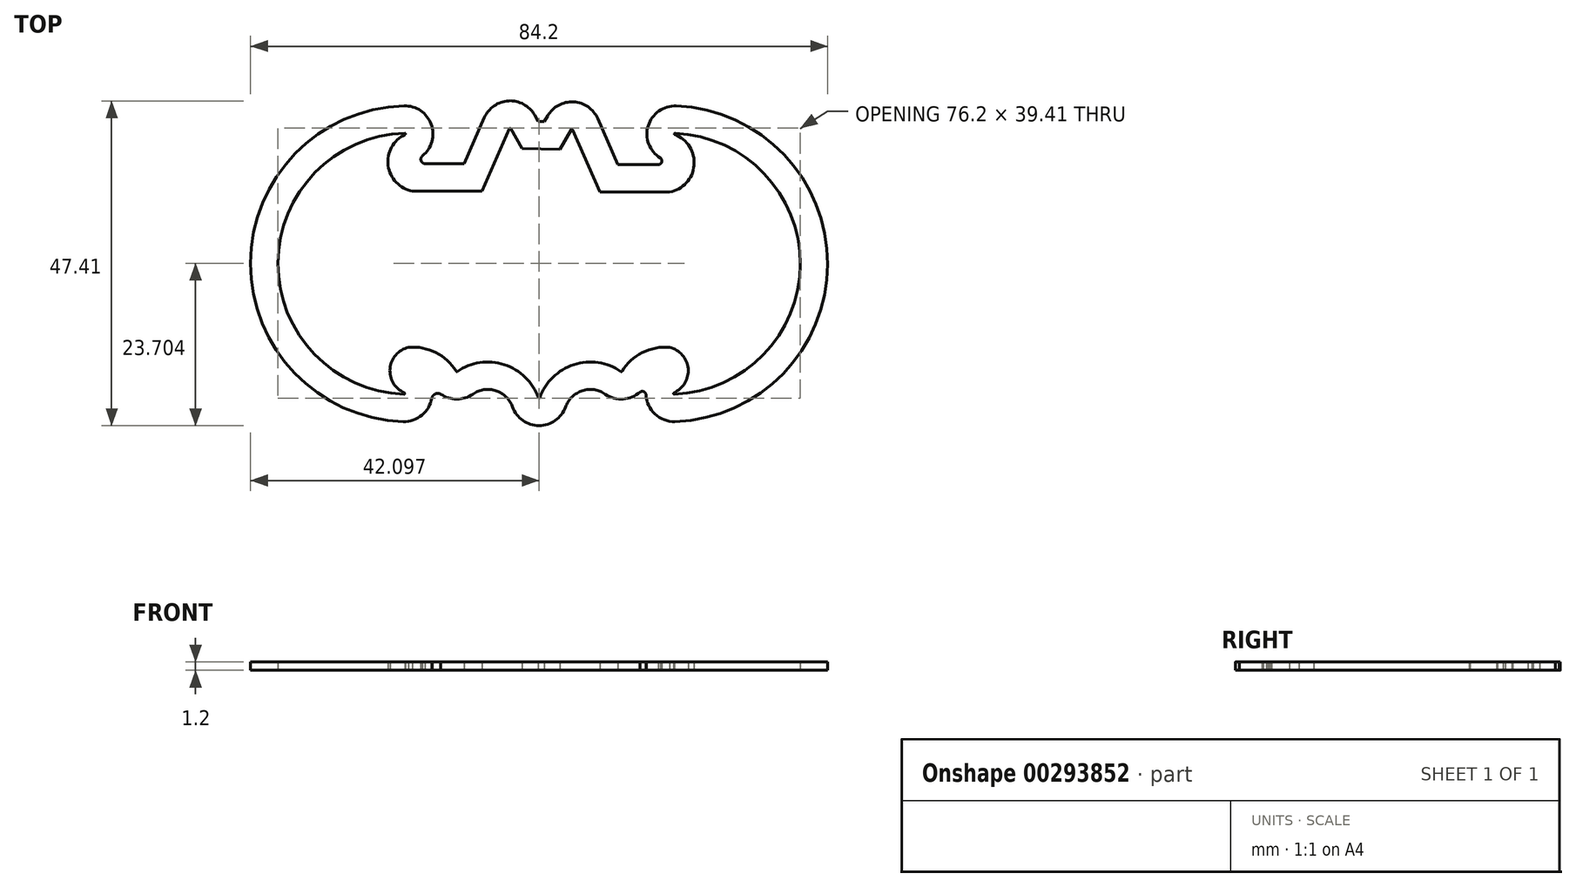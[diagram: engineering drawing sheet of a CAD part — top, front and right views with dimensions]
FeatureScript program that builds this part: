
annotation { "Feature Type Name" : "Feature", "Feature Type Description" : "" }
export const myFeature = defineFeature(function(context is Context, id is Id, definition is map)
    precondition{}
    {
        {
            var Q0;
            Q0=qCreatedBy(makeId("Top.planeOp"),FACE);
            var sketch = newSketch(context, id + "F0", { "sketchPlane" : qUnion([Q0])});
            skArc(sketch, "E0", {"start": v(-14, 19.19) * mm, "mid": v(-32.51, 0.2) * mm, "end": v(-14.11, -18.9) * mm});
            skArc(sketch, "E1", {"start": v(25.28, -18.9) * mm, "mid": v(43.69, 0.08) * mm, "end": v(25.43, 19.18) * mm});
            skArc(sketch, "E2", {"start": v(-13.96, 19) * mm, "mid": v(-16.43, 14.48) * mm, "end": v(-12.89, 10.74) * mm});
            skArc(sketch, "E3.MirrorCS", {"start": v(25.39, 18.99) * mm, "mid": v(28.2, 14.5) * mm, "end": v(24.64, 10.6) * mm});
            skArc(sketch, "E4", {"start": v(-13.46, -12.05) * mm, "mid": v(-16.16, -15.16) * mm, "end": v(-14.07, -18.7) * mm});
            skArc(sketch, "E5.MirrorCS", {"start": v(24.64, -12.05) * mm, "mid": v(27.33, -15.16) * mm, "end": v(25.24, -18.7) * mm});
            skArc(sketch, "E6", {"start": v(-6.5, -15.57) * mm, "mid": v(-9.48, -12.82) * mm, "end": v(-13.46, -12.05) * mm});
            skArc(sketch, "E7", {"start": v(5.5, -19.43) * mm, "mid": v(0.51, -14.58) * mm, "end": v(-6.36, -15.6) * mm});
            skArc(sketch, "E8.MirrorCS", {"start": v(5.68, -19.43) * mm, "mid": v(10.66, -14.58) * mm, "end": v(17.53, -15.6) * mm});
            skArc(sketch, "E9.MirrorCS", {"start": v(17.68, -15.57) * mm, "mid": v(20.66, -12.82) * mm, "end": v(24.64, -12.05) * mm});
            skLineSegment(sketch, "E10", {"start": v(-12.89, 10.74) * mm, "end": v(-2.73, 10.74) * mm});
            skLineSegment(sketch, "E11", {"start": v(-2.73, 10.74) * mm, "end": v(1.27, 19.86) * mm});
            skLineSegment(sketch, "E12", {"start": v(1.45, 19.87) * mm, "end": v(3.1, 16.98) * mm});
            skLineSegment(sketch, "E13.MirrorCS", {"start": v(10.3, 19.72) * mm, "end": v(8.65, 16.83) * mm});
            skLineSegment(sketch, "E14.MirrorCS", {"start": v(14.48, 10.6) * mm, "end": v(10.48, 19.71) * mm});
            skLineSegment(sketch, "E15.MirrorCS", {"start": v(24.64, 10.6) * mm, "end": v(14.48, 10.6) * mm});
            skLineSegment(sketch, "E16", {"start": v(3.1, 16.98) * mm, "end": v(8.65, 16.83) * mm});
            skArc(sketch, "E17.filletArc", {"start": v(5.5, -19.43) * mm, "mid": v(5.59, -19.5) * mm, "end": v(5.68, -19.43) * mm});
            skArc(sketch, "E18.filletArc", {"start": v(25.24, -18.7) * mm, "mid": v(25.18, -18.81) * mm, "end": v(25.28, -18.9) * mm});
            skArc(sketch, "E19.filletArc", {"start": v(-14.11, -18.9) * mm, "mid": v(-14, -18.81) * mm, "end": v(-14.07, -18.7) * mm});
            skArc(sketch, "E20.filletArc", {"start": v(25.43, 19.18) * mm, "mid": v(25.32, 19.1) * mm, "end": v(25.39, 18.99) * mm});
            skPoint(sketch, "E21.visualSharp", {"position": v(-13.46, 19.2) * mm});
            skArc(sketch, "E21.filletArc", {"start": v(-13.96, 19) * mm, "mid": v(-13.9, 19.11) * mm, "end": v(-14, 19.19) * mm});
            skArc(sketch, "E22.filletArc", {"start": v(1.45, 19.87) * mm, "mid": v(1.35, 19.92) * mm, "end": v(1.27, 19.86) * mm});
            skArc(sketch, "E23.filletArc", {"start": v(10.48, 19.71) * mm, "mid": v(10.4, 19.77) * mm, "end": v(10.3, 19.72) * mm});
            skPoint(sketch, "E24.visualSharp", {"position": v(-6.45, -15.66) * mm});
            skArc(sketch, "E24.filletArc", {"start": v(-6.5, -15.57) * mm, "mid": v(-6.44, -15.62) * mm, "end": v(-6.36, -15.6) * mm});
            skPoint(sketch, "E25.visualSharp", {"position": v(17.62, -15.66) * mm});
            skArc(sketch, "E25.filletArc", {"start": v(17.53, -15.6) * mm, "mid": v(17.61, -15.62) * mm, "end": v(17.68, -15.57) * mm});
            skArc(sketch, "E26.0", {"start": v(-11.43, 15.9) * mm, "mid": v(-10.15, 20.5) * mm, "end": v(-14.12, 23.19) * mm});
            skArc(sketch, "E26.1", {"start": v(25.42, -22.89) * mm, "mid": v(47.69, 0.06) * mm, "end": v(25.6, 23.18) * mm});
            skArc(sketch, "E26.2", {"start": v(21.18, -18.95) * mm, "mid": v(22.5, -21.8) * mm, "end": v(25.42, -22.89) * mm});
            skArc(sketch, "E26.4", {"start": v(15.25, -18.89) * mm, "mid": v(17.84, -19.61) * mm, "end": v(20.32, -18.57) * mm});
            skArc(sketch, "E26.5", {"start": v(9.45, -20.76) * mm, "mid": v(11.89, -18.39) * mm, "end": v(15.25, -18.89) * mm});
            skArc(sketch, "E26.6", {"start": v(1.72, -20.76) * mm, "mid": v(5.59, -23.5) * mm, "end": v(9.45, -20.76) * mm});
            skArc(sketch, "E26.7", {"start": v(-14.25, -22.89) * mm, "mid": v(-11.5, -21.96) * mm, "end": v(-10.06, -19.45) * mm});
            skArc(sketch, "E26.9", {"start": v(-8.75, -18.89) * mm, "mid": v(-6.42, -19.62) * mm, "end": v(-4.08, -18.89) * mm});
            skArc(sketch, "E26.10", {"start": v(1.72, -20.76) * mm, "mid": v(-0.72, -18.39) * mm, "end": v(-4.08, -18.89) * mm});
            skArc(sketch, "E26.11", {"start": v(25.6, 23.18) * mm, "mid": v(21.5, 20.28) * mm, "end": v(23.28, 15.59) * mm});
            skArc(sketch, "E26.12", {"start": v(-14.12, 23.19) * mm, "mid": v(-36.51, 0.21) * mm, "end": v(-14.25, -22.89) * mm});
            skLineSegment(sketch, "E26.14", {"start": v(22.97, 14.6) * mm, "end": v(17.1, 14.6) * mm});
            skLineSegment(sketch, "E26.15", {"start": v(17.1, 14.6) * mm, "end": v(14.14, 21.32) * mm});
            skArc(sketch, "E26.16", {"start": v(14.14, 21.32) * mm, "mid": v(10.6, 23.77) * mm, "end": v(6.83, 21.7) * mm});
            skLineSegment(sketch, "E26.17", {"start": v(6.83, 21.7) * mm, "end": v(6.36, 20.9) * mm});
            skLineSegment(sketch, "E26.18", {"start": v(5.45, 20.92) * mm, "end": v(6.36, 20.9) * mm});
            skLineSegment(sketch, "E26.19", {"start": v(4.92, 21.85) * mm, "end": v(5.45, 20.92) * mm});
            skArc(sketch, "E26.20", {"start": v(4.92, 21.85) * mm, "mid": v(1.14, 23.91) * mm, "end": v(-2.4, 21.47) * mm});
            skLineSegment(sketch, "E26.21", {"start": v(-5.34, 14.74) * mm, "end": v(-2.4, 21.47) * mm});
            skLineSegment(sketch, "E26.22", {"start": v(-11.06, 14.74) * mm, "end": v(-5.34, 14.74) * mm});
            skArc(sketch, "E27", {"start": v(-8.65, -18.96) * mm, "mid": v(-9.54, -18.84) * mm, "end": v(-10.08, -19.56) * mm});
            skArc(sketch, "E28", {"start": v(21.19, -19.05) * mm, "mid": v(20.9, -18.55) * mm, "end": v(20.32, -18.57) * mm});
            skArc(sketch, "E29", {"start": v(-11.43, 15.9) * mm, "mid": v(-11.62, 15.15) * mm, "end": v(-10.97, 14.74) * mm});
            skArc(sketch, "E30", {"start": v(22.9, 14.6) * mm, "mid": v(23.46, 14.95) * mm, "end": v(23.28, 15.59) * mm});
            skSolve(sketch);
        }
        {
            var Q0;
            Q0=qSketchRegion(id+"F0",true);
            extrude(context, id + "F1", {"entities" : qUnion([Q0]), "depth" : 1.2 * mm});
        }
    });
